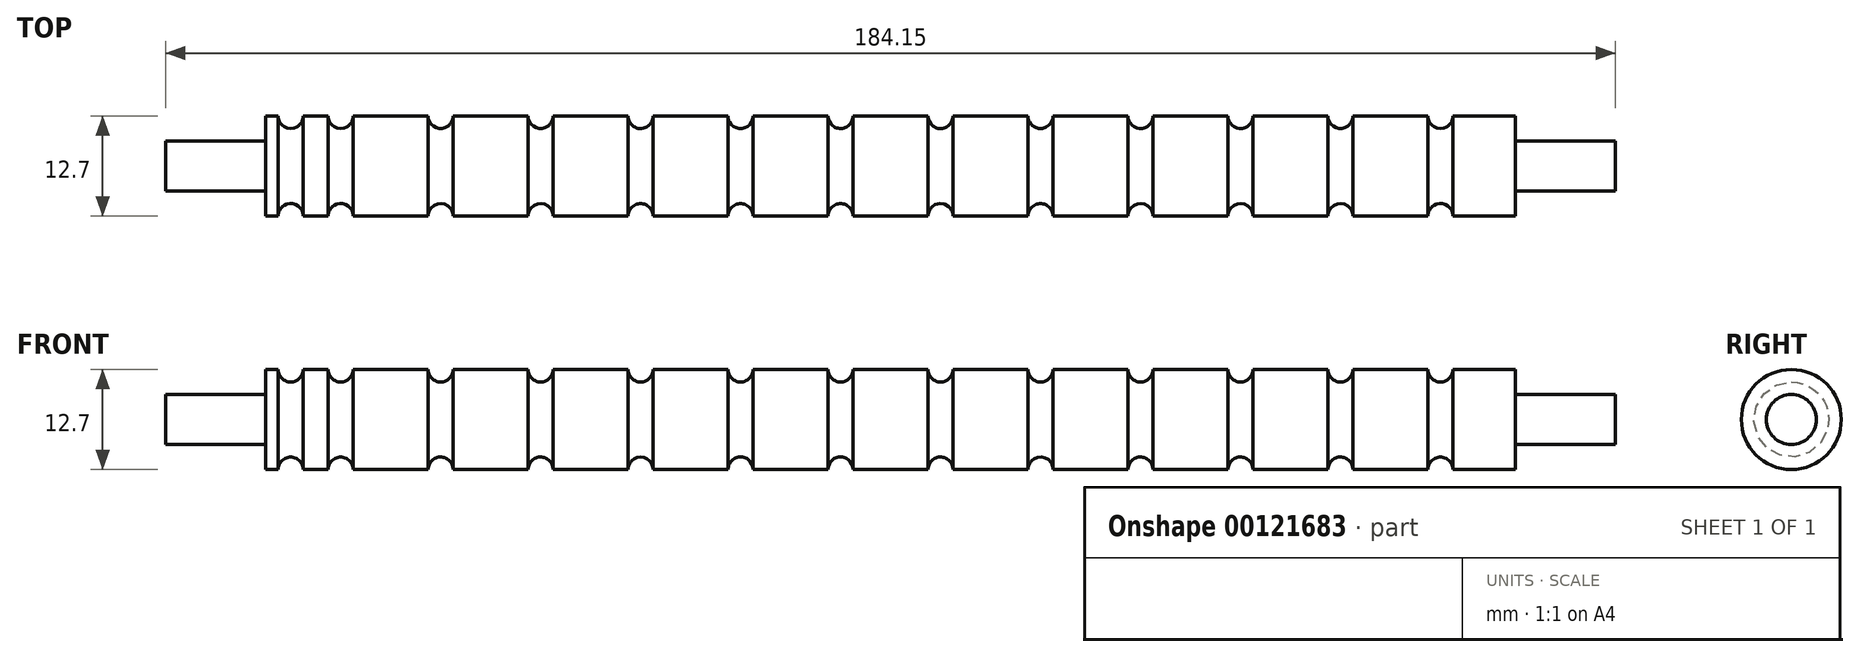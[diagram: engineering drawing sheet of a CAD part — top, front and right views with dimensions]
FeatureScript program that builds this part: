
annotation { "Feature Type Name" : "Feature", "Feature Type Description" : "" }
export const myFeature = defineFeature(function(context is Context, id is Id, definition is map)
    precondition{}
    {
        {
            var Q0;
            Q0=qCreatedBy(makeId("Front.planeOp"),FACE);
            var sketch = newSketch(context, id + "F0", { "sketchPlane" : qUnion([Q0])});
            skLineSegment(sketch, "E0.bottom", {"start": v(-76.2, 0) * mm, "end": v(82.55, 0) * mm});
            skLineSegment(sketch, "E0.top", {"start": v(-76.2, 6.35) * mm, "end": v(-74.61, 6.35) * mm});
            skLineSegment(sketch, "E0.left", {"start": v(-76.2, 0) * mm, "end": v(-76.2, 6.35) * mm});
            skLineSegment(sketch, "E0.right", {"start": v(82.55, 3.18) * mm, "end": v(82.55, 6.35) * mm});
            skArc(sketch, "E1", {"start": v(-74.61, 6.35) * mm, "mid": v(-73.03, 4.76) * mm, "end": v(-71.44, 6.35) * mm});
            skArc(sketch, "E2", {"start": v(-68.26, 6.35) * mm, "mid": v(-66.67, 4.76) * mm, "end": v(-65.09, 6.35) * mm});
            skArc(sketch, "E3", {"start": v(-55.56, 6.35) * mm, "mid": v(-53.97, 4.76) * mm, "end": v(-52.39, 6.35) * mm});
            skArc(sketch, "E4", {"start": v(-42.86, 6.35) * mm, "mid": v(-41.27, 4.76) * mm, "end": v(-39.69, 6.35) * mm});
            skArc(sketch, "E5", {"start": v(-30.16, 6.35) * mm, "mid": v(-28.57, 4.76) * mm, "end": v(-26.99, 6.35) * mm});
            skArc(sketch, "E6", {"start": v(-17.46, 6.35) * mm, "mid": v(-15.87, 4.76) * mm, "end": v(-14.29, 6.35) * mm});
            skArc(sketch, "E7", {"start": v(-4.76, 6.35) * mm, "mid": v(-3.17, 4.76) * mm, "end": v(-1.59, 6.35) * mm});
            skArc(sketch, "E8", {"start": v(7.94, 6.35) * mm, "mid": v(9.53, 4.76) * mm, "end": v(11.11, 6.35) * mm});
            skArc(sketch, "E9", {"start": v(20.64, 6.35) * mm, "mid": v(22.23, 4.76) * mm, "end": v(23.81, 6.35) * mm});
            skArc(sketch, "E10", {"start": v(33.34, 6.35) * mm, "mid": v(34.93, 4.76) * mm, "end": v(36.51, 6.35) * mm});
            skArc(sketch, "E11", {"start": v(46.04, 6.35) * mm, "mid": v(47.63, 4.76) * mm, "end": v(49.21, 6.35) * mm});
            skArc(sketch, "E12", {"start": v(58.74, 6.35) * mm, "mid": v(60.33, 4.76) * mm, "end": v(61.91, 6.35) * mm});
            skArc(sketch, "E13", {"start": v(71.44, 6.35) * mm, "mid": v(73.03, 4.76) * mm, "end": v(74.61, 6.35) * mm});
            skLineSegment(sketch, "E14", {"start": v(82.55, 3.18) * mm, "end": v(95.25, 3.18) * mm});
            skPoint(sketch, "E14.endSnap0", {"position": v(82.55, 3.18) * mm});
            skLineSegment(sketch, "E15", {"start": v(82.55, 0) * mm, "end": v(95.25, 0) * mm});
            skLineSegment(sketch, "E16", {"start": v(95.25, 0) * mm, "end": v(95.25, 3.18) * mm});
            skLineSegment(sketch, "E17", {"start": v(-76.2, 0) * mm, "end": v(-88.9, 0) * mm});
            skLineSegment(sketch, "E18", {"start": v(-88.9, 0) * mm, "end": v(-88.9, 3.17) * mm});
            skPoint(sketch, "E19.start.orphan", {"position": v(-76.2, 3.18) * mm});
            skLineSegment(sketch, "E20", {"start": v(-76.2, 3.18) * mm, "end": v(-88.9, 3.17) * mm});
            skLineSegment(sketch, "E21.trimOffspring", {"start": v(-52.39, 6.35) * mm, "end": v(-42.86, 6.35) * mm});
            skLineSegment(sketch, "E22.trimOffspring", {"start": v(-39.69, 6.35) * mm, "end": v(-30.16, 6.35) * mm});
            skLineSegment(sketch, "E23.trimOffspring", {"start": v(-26.99, 6.35) * mm, "end": v(-17.46, 6.35) * mm});
            skLineSegment(sketch, "E24.trimOffspring", {"start": v(-1.59, 6.35) * mm, "end": v(7.94, 6.35) * mm});
            skLineSegment(sketch, "E25.trimOffspring", {"start": v(11.11, 6.35) * mm, "end": v(20.64, 6.35) * mm});
            skLineSegment(sketch, "E26.trimOffspring", {"start": v(23.81, 6.35) * mm, "end": v(33.34, 6.35) * mm});
            skLineSegment(sketch, "E27.trimOffspring", {"start": v(36.51, 6.35) * mm, "end": v(46.04, 6.35) * mm});
            skLineSegment(sketch, "E28.trimOffspring", {"start": v(49.21, 6.35) * mm, "end": v(58.74, 6.35) * mm});
            skLineSegment(sketch, "E29.trimOffspring", {"start": v(61.91, 6.35) * mm, "end": v(71.44, 6.35) * mm});
            skLineSegment(sketch, "E30.trimOffspring", {"start": v(74.61, 6.35) * mm, "end": v(82.55, 6.35) * mm});
            skLineSegment(sketch, "E31", {"start": v(-14.29, 6.35) * mm, "end": v(-4.76, 6.35) * mm});
            skLineSegment(sketch, "E32", {"start": v(-71.44, 6.35) * mm, "end": v(-68.26, 6.35) * mm});
            skLineSegment(sketch, "E33", {"start": v(-65.09, 6.35) * mm, "end": v(-55.56, 6.35) * mm});
            skSolve(sketch);
        }
        {
            var Q0;
            Q0 = qSketchRegion(id + "F0", true);
            var Q1;
            Q1=sQuery(id+"F0.wireOp",EDGE,"E0.bottom");
            revolve(context, id + "F1", {"entities" : qUnion([Q0]), "axis" : qUnion([Q1]), "revolveType" : RevolveType.FULL});
        }
    });
